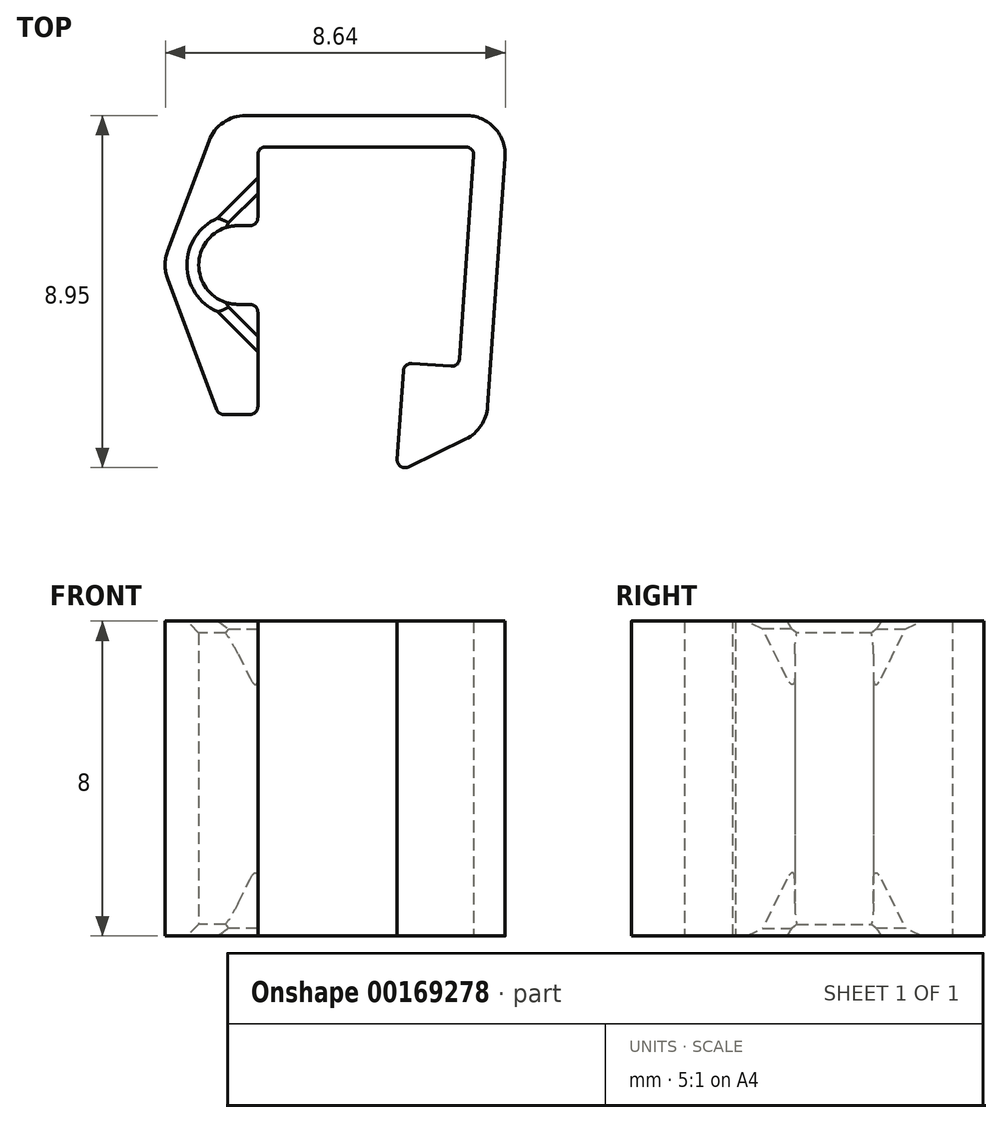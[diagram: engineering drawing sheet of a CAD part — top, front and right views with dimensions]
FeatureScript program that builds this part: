
annotation { "Feature Type Name" : "Feature", "Feature Type Description" : "" }
export const myFeature = defineFeature(function(context is Context, id is Id, definition is map)
    precondition{}
    {
        {
            var Q0;
            Q0=qCreatedBy(makeId("Top.planeOp"),FACE);
            var sketch = newSketch(context, id + "F0", { "sketchPlane" : qUnion([Q0])});
            skLineSegment(sketch, "E0", {"start": v(0, 0) * mm, "end": v(-0.4, -5.59) * mm});
            skLineSegment(sketch, "E1", {"start": v(-0.4, -5.59) * mm, "end": v(-1.79, -5.49) * mm});
            skLineSegment(sketch, "E2", {"start": v(-1.79, -5.49) * mm, "end": v(-1.98, -8.28) * mm});
            skLineSegment(sketch, "E3", {"start": v(-1.98, -8.28) * mm, "end": v(0.3, -7.17) * mm});
            skLineSegment(sketch, "E4", {"start": v(0.3, -7.17) * mm, "end": v(0.86, 0.8) * mm});
            skLineSegment(sketch, "E5", {"start": v(0.86, 0.8) * mm, "end": v(-6.5, 0.8) * mm});
            skLineSegment(sketch, "E6", {"start": v(-6, -4) * mm, "end": v(-5.5, -4) * mm});
            skLineSegment(sketch, "E7", {"start": v(-5.5, -4) * mm, "end": v(-5.5, -6.8) * mm});
            skLineSegment(sketch, "E8", {"start": v(-7.92, -3) * mm, "end": v(-6.5, -6.8) * mm});
            skLineSegment(sketch, "E9", {"start": v(-6.5, -6.8) * mm, "end": v(-5.5, -6.8) * mm});
            skLineSegment(sketch, "E10", {"start": v(-5.5, -2) * mm, "end": v(-6, -2) * mm});
            skLineSegment(sketch, "E11", {"start": v(0, 0) * mm, "end": v(-5.5, 0) * mm});
            skLineSegment(sketch, "E12", {"start": v(-5.5, 0) * mm, "end": v(-5.5, -2) * mm});
            skArc(sketch, "E13", {"start": v(-6, -2) * mm, "mid": v(-7, -3) * mm, "end": v(-6, -4) * mm});
            skLineSegment(sketch, "E14", {"start": v(-7.92, -3) * mm, "end": v(-6.5, 0.8) * mm});
            skLineSegment(sketch, "E15", {"start": v(-6.5, -6.8) * mm, "end": v(-6.5, 0.8) * mm, "construction": true});
            skLineSegment(sketch, "E16", {"start": v(-6, -3) * mm, "end": v(-6.94, -2.65) * mm, "construction": true});
            skLineSegment(sketch, "E17", {"start": v(-6.94, -2.65) * mm, "end": v(-7.69, -2.37) * mm, "construction": true});
            skLineSegment(sketch, "E18", {"start": v(0, 0) * mm, "end": v(0, 0.8) * mm, "construction": true});
            skLineSegment(sketch, "E19", {"start": v(0.8, -0.06) * mm, "end": v(0, 0) * mm, "construction": true});
            skSolve(sketch);
        }
        {
            var Q0;
            Q0=qSketchRegion(id+"F0",true);
            extrude(context, id + "F1", {"entities" : qUnion([Q0]), "depth" : 4 * mm});
        }
        {
            var Q0;
            Q0=makeQuery(id+"F1.opExtrude","CAP_FACE",FACE,{"disambiguationData":[OSD([sQuery(id+"F0.wireOp",EDGE,"E0"),sQuery(id+"F0.wireOp",EDGE,"E1"),sQuery(id+"F0.wireOp",EDGE,"E2"),sQuery(id+"F0.wireOp",EDGE,"E3"),sQuery(id+"F0.wireOp",EDGE,"E4"),sQuery(id+"F0.wireOp",EDGE,"E5"),sQuery(id+"F0.wireOp",EDGE,"3qQk4eZ2-qFBK-7vCE-47k8-9gwiF50xY8QG"),sQuery(id+"F0.wireOp",EDGE,"FwfflrWr-MbD4-lGZ7-AJjG-6BkzjliF19me"),sQuery(id+"F0.wireOp",EDGE,"E6"),sQuery(id+"F0.wireOp",EDGE,"E7"),sQuery(id+"F0.wireOp",EDGE,"dEJFUDGW-VdPt-nXIw-TINV-OlQtnsbTHH9Y"),sQuery(id+"F0.wireOp",EDGE,"E8"),sQuery(id+"F0.wireOp",EDGE,"E9")])],"isStart":false});
            var sketch = newSketch(context, id + "F2", { "sketchPlane" : qUnion([Q0])});
            skLineSegment(sketch, "E20", {"start": v(-6.7, -3.7) * mm, "end": v(-5.5, -4.91) * mm});
            skLineSegment(sketch, "E21", {"start": v(-5.5, -4.91) * mm, "end": v(-5.5, -4) * mm});
            skLineSegment(sketch, "E22", {"start": v(-5.5, -4) * mm, "end": v(-6.7, -3.7) * mm});
            skLineSegment(sketch, "E23", {"start": v(-6.7, -2.3) * mm, "end": v(-5.5, -1.09) * mm});
            skLineSegment(sketch, "E24", {"start": v(-5.5, -1.09) * mm, "end": v(-5.5, -2) * mm});
            skLineSegment(sketch, "E25", {"start": v(-5.5, -2) * mm, "end": v(-6.7, -2.3) * mm});
            skSolve(sketch);
        }
        {
            var Q0;
            Q0=qSketchRegion(id+"F2",true);
            extrude(context, id + "F3", {"entities" : qUnion([Q0]), "operationType" : NewBodyOperationType.REMOVE, "oppositeDirection" : true, "depth" : 2 * mm});
        }
        {
            var Q0;
            Q0=makeQuery(id+"F3.boolean.opBoolean","COPY",EDGE,{"derivedFrom":makeQuery(id+"F3.opExtrude","CAP_EDGE",EDGE,{"disambiguationData":[OSD([sQuery(id+"F2.wireOp",EDGE,"E20")])],"isStart":false})});
            chamfer(context, id + "F4", {"entities" : qUnion([Q0]), "chamferType" : ChamferType.TWO_OFFSETS, "width1" : .7 * mm, "oppositeDirection" : false, "width2" : 2 * mm, "tangentPropagation" : true});
        }
        {
            var Q0;
            Q0=makeQuery(id+"F3.boolean.opBoolean","COPY",EDGE,{"derivedFrom":makeQuery(id+"F3.opExtrude","CAP_EDGE",EDGE,{"disambiguationData":[OSD([sQuery(id+"F2.wireOp",EDGE,"E23")])],"isStart":false})});
            chamfer(context, id + "F5", {"entities" : qUnion([Q0]), "chamferType" : ChamferType.TWO_OFFSETS, "width1" : 2 * mm, "oppositeDirection" : false, "width2" : .7 * mm, "tangentPropagation" : true});
        }
        {
            var Q0;
            Q0=makeQuery(id+"F1.opExtrude","SWEPT_EDGE",EDGE,{"disambiguationData":[OSD([sQuery(id+"F0.wireOp",EDGE,"E0"),sQuery(id+"F0.wireOp",EDGE,"3qQk4eZ2-qFBK-7vCE-47k8-9gwiF50xY8QG")])]});
            var Q1;
            Q1=makeQuery(id+"F1.opExtrude","SWEPT_EDGE",EDGE,{"disambiguationData":[OSD([sQuery(id+"F0.wireOp",EDGE,"E0"),sQuery(id+"F0.wireOp",EDGE,"E1")])]});
            var Q2;
            Q2=makeQuery(id+"F1.opExtrude","SWEPT_EDGE",EDGE,{"disambiguationData":[OSD([sQuery(id+"F0.wireOp",EDGE,"E1"),sQuery(id+"F0.wireOp",EDGE,"E2")])]});
            var Q3;
            Q3=makeQuery(id+"F1.opExtrude","SWEPT_EDGE",EDGE,{"disambiguationData":[OSD([sQuery(id+"F0.wireOp",EDGE,"E2"),sQuery(id+"F0.wireOp",EDGE,"E3")])]});
            var Q4;
            Q4=makeQuery(id+"F1.opExtrude","SWEPT_EDGE",EDGE,{"disambiguationData":[OSD([sQuery(id+"F0.wireOp",EDGE,"E7"),sQuery(id+"F0.wireOp",EDGE,"E9")])]});
            var Q5;
            Q5=makeQuery(id+"F1.opExtrude","SWEPT_EDGE",EDGE,{"disambiguationData":[OSD([sQuery(id+"F0.wireOp",EDGE,"E6"),sQuery(id+"F0.wireOp",EDGE,"E7")])]});
            var Q6;
            Q6=makeQuery(id+"F1.opExtrude","SWEPT_EDGE",EDGE,{"disambiguationData":[OSD([sQuery(id+"F0.wireOp",EDGE,"E10"),sQuery(id+"F0.wireOp",EDGE,"E12")])]});
            var Q7;
            Q7=makeQuery(id+"F1.opExtrude","SWEPT_EDGE",EDGE,{"disambiguationData":[OSD([sQuery(id+"F0.wireOp",EDGE,"E8"),sQuery(id+"F0.wireOp",EDGE,"E9")])]});
            var Q8;
            Q8=makeQuery(id+"F1.opExtrude","SWEPT_EDGE",EDGE,{"disambiguationData":[OSD([sQuery(id+"F0.wireOp",EDGE,"E11"),sQuery(id+"F0.wireOp",EDGE,"E12")])]});
            fillet(context, id + "F6", {"entities" : qUnion([Q0, Q1, Q2, Q3, Q4, Q5, Q6, Q7, Q8]), "radius" : .2 * mm, "tangentPropagation" : true, "allowEdgeOverflow" : false});
        }
        {
            var Q0;
            Q0=makeQuery(id+"F1.opExtrude","SWEPT_EDGE",EDGE,{"disambiguationData":[OSD([sQuery(id+"F0.wireOp",EDGE,"E4"),sQuery(id+"F0.wireOp",EDGE,"E5")])]});
            var Q1;
            Q1=makeQuery(id+"F1.opExtrude","SWEPT_EDGE",EDGE,{"disambiguationData":[OSD([sQuery(id+"F0.wireOp",EDGE,"E3"),sQuery(id+"F0.wireOp",EDGE,"E4")])]});
            var Q2;
            Q2=makeQuery(id+"F1.opExtrude","SWEPT_EDGE",EDGE,{"disambiguationData":[OSD([sQuery(id+"F0.wireOp",EDGE,"E8"),sQuery(id+"F0.wireOp",EDGE,"E9")])]});
            var Q3;
            Q3=makeQuery(id+"F1.opExtrude","SWEPT_EDGE",EDGE,{"disambiguationData":[OSD([sQuery(id+"F0.wireOp",EDGE,"E8"),sQuery(id+"F0.wireOp",EDGE,"E14")])]});
            var Q4;
            Q4=makeQuery(id+"F1.opExtrude","SWEPT_EDGE",EDGE,{"disambiguationData":[OSD([sQuery(id+"F0.wireOp",EDGE,"E5"),sQuery(id+"F0.wireOp",EDGE,"E14")])]});
            fillet(context, id + "F7", {"entities" : qUnion([Q0, Q1, Q2, Q3, Q4]), "radius" : 1 * mm, "tangentPropagation" : true, "allowEdgeOverflow" : false});
        }
        {
            var Q0;
            Q0=makeQuery(id+"F1.opExtrude","SWEPT_BODY",BODY,{"disambiguationData":[OSD([sQuery(id+"F0.wireOp",EDGE,"E0"),sQuery(id+"F0.wireOp",EDGE,"E1"),sQuery(id+"F0.wireOp",EDGE,"E2"),sQuery(id+"F0.wireOp",EDGE,"E3"),sQuery(id+"F0.wireOp",EDGE,"E4"),sQuery(id+"F0.wireOp",EDGE,"E5"),sQuery(id+"F0.wireOp",EDGE,"3qQk4eZ2-qFBK-7vCE-47k8-9gwiF50xY8QG"),sQuery(id+"F0.wireOp",EDGE,"FwfflrWr-MbD4-lGZ7-AJjG-6BkzjliF19me"),sQuery(id+"F0.wireOp",EDGE,"E6"),sQuery(id+"F0.wireOp",EDGE,"E7"),sQuery(id+"F0.wireOp",EDGE,"dEJFUDGW-VdPt-nXIw-TINV-OlQtnsbTHH9Y"),sQuery(id+"F0.wireOp",EDGE,"E8"),sQuery(id+"F0.wireOp",EDGE,"E9")])]});
            var Q1;
            Q1=makeQuery(id+"F1.opExtrude","CAP_FACE",FACE,{"disambiguationData":[OSD([sQuery(id+"F0.wireOp",EDGE,"E0"),sQuery(id+"F0.wireOp",EDGE,"E1"),sQuery(id+"F0.wireOp",EDGE,"E2"),sQuery(id+"F0.wireOp",EDGE,"E3"),sQuery(id+"F0.wireOp",EDGE,"E4"),sQuery(id+"F0.wireOp",EDGE,"E5"),sQuery(id+"F0.wireOp",EDGE,"3qQk4eZ2-qFBK-7vCE-47k8-9gwiF50xY8QG"),sQuery(id+"F0.wireOp",EDGE,"FwfflrWr-MbD4-lGZ7-AJjG-6BkzjliF19me"),sQuery(id+"F0.wireOp",EDGE,"E6"),sQuery(id+"F0.wireOp",EDGE,"E7"),sQuery(id+"F0.wireOp",EDGE,"dEJFUDGW-VdPt-nXIw-TINV-OlQtnsbTHH9Y"),sQuery(id+"F0.wireOp",EDGE,"E8"),sQuery(id+"F0.wireOp",EDGE,"E9")])],"isStart":true});
            mirror(context, id + "F8", {"operationType" : NewBodyOperationType.ADD, "entities" : qUnion([Q0]), "mirrorPlane" : qUnion([Q1])});
        }
        {
            var Q0;
            Q0=makeQuery(id+"F1.opExtrude","CAP_EDGE",EDGE,{"disambiguationData":[OSD([sQuery(id+"F0.wireOp",EDGE,"E13")])],"isStart":false});
            var Q1;
            Q1=makeQuery(id+"F5.opChamfer","BLEND_EDGE",EDGE,{"blendedFrom":[makeQuery(id+"F3.boolean.opBoolean","COPY",EDGE,{"derivedFrom":makeQuery(id+"F3.opExtrude","CAP_EDGE",EDGE,{"disambiguationData":[OSD([sQuery(id+"F2.wireOp",EDGE,"E23")])],"isStart":false})}),makeQuery(id+"F1.opExtrude","CAP_FACE",FACE,{"disambiguationData":[OSD([sQuery(id+"F0.wireOp",EDGE,"E0"),sQuery(id+"F0.wireOp",EDGE,"E1"),sQuery(id+"F0.wireOp",EDGE,"E2"),sQuery(id+"F0.wireOp",EDGE,"E3"),sQuery(id+"F0.wireOp",EDGE,"E4"),sQuery(id+"F0.wireOp",EDGE,"E5"),sQuery(id+"F0.wireOp",EDGE,"E6"),sQuery(id+"F0.wireOp",EDGE,"E7"),sQuery(id+"F0.wireOp",EDGE,"E8"),sQuery(id+"F0.wireOp",EDGE,"E9"),sQuery(id+"F0.wireOp",EDGE,"E10"),sQuery(id+"F0.wireOp",EDGE,"E11"),sQuery(id+"F0.wireOp",EDGE,"E12"),sQuery(id+"F0.wireOp",EDGE,"E13"),sQuery(id+"F0.wireOp",EDGE,"E14")])],"isStart":false})],"blendedInto":[makeQuery(id+"F1.opExtrude","CAP_FACE",FACE,{"disambiguationData":[OSD([sQuery(id+"F0.wireOp",EDGE,"E0"),sQuery(id+"F0.wireOp",EDGE,"E1"),sQuery(id+"F0.wireOp",EDGE,"E2"),sQuery(id+"F0.wireOp",EDGE,"E3"),sQuery(id+"F0.wireOp",EDGE,"E4"),sQuery(id+"F0.wireOp",EDGE,"E5"),sQuery(id+"F0.wireOp",EDGE,"E6"),sQuery(id+"F0.wireOp",EDGE,"E7"),sQuery(id+"F0.wireOp",EDGE,"E8"),sQuery(id+"F0.wireOp",EDGE,"E9"),sQuery(id+"F0.wireOp",EDGE,"E10"),sQuery(id+"F0.wireOp",EDGE,"E11"),sQuery(id+"F0.wireOp",EDGE,"E12"),sQuery(id+"F0.wireOp",EDGE,"E13"),sQuery(id+"F0.wireOp",EDGE,"E14")])],"isStart":false})]});
            var Q2;
            Q2=makeQuery(id+"F4.opChamfer","BLEND_EDGE",EDGE,{"blendedFrom":[makeQuery(id+"F3.boolean.opBoolean","COPY",EDGE,{"derivedFrom":makeQuery(id+"F3.opExtrude","CAP_EDGE",EDGE,{"disambiguationData":[OSD([sQuery(id+"F2.wireOp",EDGE,"E20")])],"isStart":false})}),makeQuery(id+"F1.opExtrude","CAP_FACE",FACE,{"disambiguationData":[OSD([sQuery(id+"F0.wireOp",EDGE,"E0"),sQuery(id+"F0.wireOp",EDGE,"E1"),sQuery(id+"F0.wireOp",EDGE,"E2"),sQuery(id+"F0.wireOp",EDGE,"E3"),sQuery(id+"F0.wireOp",EDGE,"E4"),sQuery(id+"F0.wireOp",EDGE,"E5"),sQuery(id+"F0.wireOp",EDGE,"E6"),sQuery(id+"F0.wireOp",EDGE,"E7"),sQuery(id+"F0.wireOp",EDGE,"E8"),sQuery(id+"F0.wireOp",EDGE,"E9"),sQuery(id+"F0.wireOp",EDGE,"E10"),sQuery(id+"F0.wireOp",EDGE,"E11"),sQuery(id+"F0.wireOp",EDGE,"E12"),sQuery(id+"F0.wireOp",EDGE,"E13"),sQuery(id+"F0.wireOp",EDGE,"E14")])],"isStart":false})],"blendedInto":[makeQuery(id+"F1.opExtrude","CAP_FACE",FACE,{"disambiguationData":[OSD([sQuery(id+"F0.wireOp",EDGE,"E0"),sQuery(id+"F0.wireOp",EDGE,"E1"),sQuery(id+"F0.wireOp",EDGE,"E2"),sQuery(id+"F0.wireOp",EDGE,"E3"),sQuery(id+"F0.wireOp",EDGE,"E4"),sQuery(id+"F0.wireOp",EDGE,"E5"),sQuery(id+"F0.wireOp",EDGE,"E6"),sQuery(id+"F0.wireOp",EDGE,"E7"),sQuery(id+"F0.wireOp",EDGE,"E8"),sQuery(id+"F0.wireOp",EDGE,"E9"),sQuery(id+"F0.wireOp",EDGE,"E10"),sQuery(id+"F0.wireOp",EDGE,"E11"),sQuery(id+"F0.wireOp",EDGE,"E12"),sQuery(id+"F0.wireOp",EDGE,"E13"),sQuery(id+"F0.wireOp",EDGE,"E14")])],"isStart":false})]});
            var Q3;
            Q3=makeQuery(id+"F8.opPattern","COPY",EDGE,{"derivedFrom":makeQuery(id+"F1.opExtrude","CAP_EDGE",EDGE,{"disambiguationData":[OSD([sQuery(id+"F0.wireOp",EDGE,"E13")])],"isStart":false}),"instanceName":"1"});
            var Q4;
            Q4=makeQuery(id+"F8.opPattern","COPY",EDGE,{"derivedFrom":makeQuery(id+"F5.opChamfer","BLEND_EDGE",EDGE,{"blendedFrom":[makeQuery(id+"F3.boolean.opBoolean","COPY",EDGE,{"derivedFrom":makeQuery(id+"F3.opExtrude","CAP_EDGE",EDGE,{"disambiguationData":[OSD([sQuery(id+"F2.wireOp",EDGE,"E23")])],"isStart":false})}),makeQuery(id+"F1.opExtrude","CAP_FACE",FACE,{"disambiguationData":[OSD([sQuery(id+"F0.wireOp",EDGE,"E0"),sQuery(id+"F0.wireOp",EDGE,"E1"),sQuery(id+"F0.wireOp",EDGE,"E2"),sQuery(id+"F0.wireOp",EDGE,"E3"),sQuery(id+"F0.wireOp",EDGE,"E4"),sQuery(id+"F0.wireOp",EDGE,"E5"),sQuery(id+"F0.wireOp",EDGE,"E6"),sQuery(id+"F0.wireOp",EDGE,"E7"),sQuery(id+"F0.wireOp",EDGE,"E8"),sQuery(id+"F0.wireOp",EDGE,"E9"),sQuery(id+"F0.wireOp",EDGE,"E10"),sQuery(id+"F0.wireOp",EDGE,"E11"),sQuery(id+"F0.wireOp",EDGE,"E12"),sQuery(id+"F0.wireOp",EDGE,"E13"),sQuery(id+"F0.wireOp",EDGE,"E14")])],"isStart":false})],"blendedInto":[makeQuery(id+"F1.opExtrude","CAP_FACE",FACE,{"disambiguationData":[OSD([sQuery(id+"F0.wireOp",EDGE,"E0"),sQuery(id+"F0.wireOp",EDGE,"E1"),sQuery(id+"F0.wireOp",EDGE,"E2"),sQuery(id+"F0.wireOp",EDGE,"E3"),sQuery(id+"F0.wireOp",EDGE,"E4"),sQuery(id+"F0.wireOp",EDGE,"E5"),sQuery(id+"F0.wireOp",EDGE,"E6"),sQuery(id+"F0.wireOp",EDGE,"E7"),sQuery(id+"F0.wireOp",EDGE,"E8"),sQuery(id+"F0.wireOp",EDGE,"E9"),sQuery(id+"F0.wireOp",EDGE,"E10"),sQuery(id+"F0.wireOp",EDGE,"E11"),sQuery(id+"F0.wireOp",EDGE,"E12"),sQuery(id+"F0.wireOp",EDGE,"E13"),sQuery(id+"F0.wireOp",EDGE,"E14")])],"isStart":false})]}),"instanceName":"1"});
            var Q5;
            Q5=makeQuery(id+"F8.opPattern","COPY",EDGE,{"derivedFrom":makeQuery(id+"F4.opChamfer","BLEND_EDGE",EDGE,{"blendedFrom":[makeQuery(id+"F3.boolean.opBoolean","COPY",EDGE,{"derivedFrom":makeQuery(id+"F3.opExtrude","CAP_EDGE",EDGE,{"disambiguationData":[OSD([sQuery(id+"F2.wireOp",EDGE,"E20")])],"isStart":false})}),makeQuery(id+"F1.opExtrude","CAP_FACE",FACE,{"disambiguationData":[OSD([sQuery(id+"F0.wireOp",EDGE,"E0"),sQuery(id+"F0.wireOp",EDGE,"E1"),sQuery(id+"F0.wireOp",EDGE,"E2"),sQuery(id+"F0.wireOp",EDGE,"E3"),sQuery(id+"F0.wireOp",EDGE,"E4"),sQuery(id+"F0.wireOp",EDGE,"E5"),sQuery(id+"F0.wireOp",EDGE,"E6"),sQuery(id+"F0.wireOp",EDGE,"E7"),sQuery(id+"F0.wireOp",EDGE,"E8"),sQuery(id+"F0.wireOp",EDGE,"E9"),sQuery(id+"F0.wireOp",EDGE,"E10"),sQuery(id+"F0.wireOp",EDGE,"E11"),sQuery(id+"F0.wireOp",EDGE,"E12"),sQuery(id+"F0.wireOp",EDGE,"E13"),sQuery(id+"F0.wireOp",EDGE,"E14")])],"isStart":false})],"blendedInto":[makeQuery(id+"F1.opExtrude","CAP_FACE",FACE,{"disambiguationData":[OSD([sQuery(id+"F0.wireOp",EDGE,"E0"),sQuery(id+"F0.wireOp",EDGE,"E1"),sQuery(id+"F0.wireOp",EDGE,"E2"),sQuery(id+"F0.wireOp",EDGE,"E3"),sQuery(id+"F0.wireOp",EDGE,"E4"),sQuery(id+"F0.wireOp",EDGE,"E5"),sQuery(id+"F0.wireOp",EDGE,"E6"),sQuery(id+"F0.wireOp",EDGE,"E7"),sQuery(id+"F0.wireOp",EDGE,"E8"),sQuery(id+"F0.wireOp",EDGE,"E9"),sQuery(id+"F0.wireOp",EDGE,"E10"),sQuery(id+"F0.wireOp",EDGE,"E11"),sQuery(id+"F0.wireOp",EDGE,"E12"),sQuery(id+"F0.wireOp",EDGE,"E13"),sQuery(id+"F0.wireOp",EDGE,"E14")])],"isStart":false})]}),"instanceName":"1"});
            chamfer(context, id + "F9", {"entities" : qUnion([Q0, Q1, Q2, Q3, Q4, Q5]), "chamferType" : ChamferType.OFFSET_ANGLE, "width" : .3 * mm, "oppositeDirection" : false, "angle" : 45 * degree, "tangentPropagation" : true});
        }
    });
